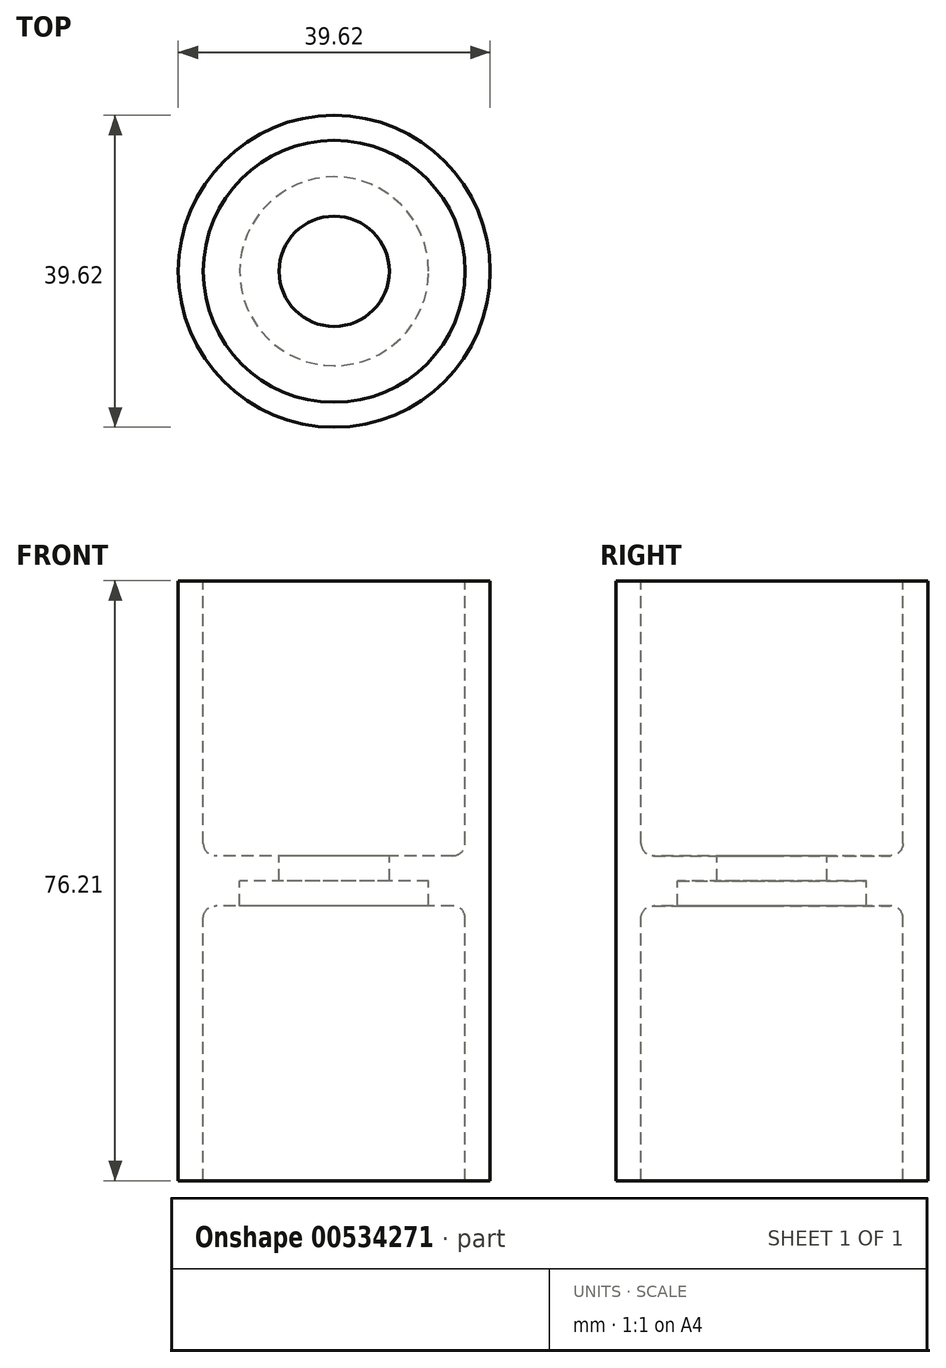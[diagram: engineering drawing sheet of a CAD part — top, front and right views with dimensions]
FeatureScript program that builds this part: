
annotation { "Feature Type Name" : "Feature", "Feature Type Description" : "" }
export const myFeature = defineFeature(function(context is Context, id is Id, definition is map)
    precondition{}
    {
        {
            var Q0;
            Q0=qCreatedBy(makeId("Front.planeOp"),FACE);
            var sketch = newSketch(context, id + "F0", { "sketchPlane" : qUnion([Q0])});
            skLineSegment(sketch, "E0", {"start": v(0, 40.97) * mm, "end": v(0, -48.47) * mm, "construction": true});
            skLineSegment(sketch, "E1", {"start": v(-19.81, 41.28) * mm, "end": v(-16.64, 41.28) * mm});
            skLineSegment(sketch, "E2", {"start": v(-16.64, 41.27) * mm, "end": v(-16.64, 7.94) * mm});
            skLineSegment(sketch, "E3", {"start": v(-15.05, 6.35) * mm, "end": v(-7, 6.35) * mm});
            skLineSegment(sketch, "E4", {"start": v(-7, 6.35) * mm, "end": v(-7, 3.18) * mm});
            skLineSegment(sketch, "E5", {"start": v(-7, 3.18) * mm, "end": v(-12, 3.17) * mm});
            skLineSegment(sketch, "E6", {"start": v(-12, 3.18) * mm, "end": v(-12, 0) * mm});
            skLineSegment(sketch, "E7", {"start": v(-12, 0) * mm, "end": v(-15.05, 0) * mm});
            skLineSegment(sketch, "E8", {"start": v(-16.64, -1.59) * mm, "end": v(-16.64, -34.93) * mm});
            skLineSegment(sketch, "E9", {"start": v(-16.64, -34.92) * mm, "end": v(-19.81, -34.92) * mm});
            skLineSegment(sketch, "E10", {"start": v(-19.81, -34.92) * mm, "end": v(-19.81, 41.28) * mm});
            skPoint(sketch, "E11.visualSharp", {"position": v(-16.64, 6.35) * mm});
            skArc(sketch, "E11.filletArc", {"start": v(-16.64, 7.94) * mm, "mid": v(-16.17, 6.81) * mm, "end": v(-15.05, 6.35) * mm});
            skPoint(sketch, "E12.visualSharp", {"position": v(-16.64, 0) * mm});
            skArc(sketch, "E12.filletArc", {"start": v(-15.05, 0) * mm, "mid": v(-16.17, -0.46) * mm, "end": v(-16.64, -1.59) * mm});
            skSolve(sketch);
        }
        {
            var Q0;
            Q0=makeQuery(id+"F0.imprint","IMPRINT",FACE,{"disambiguationData":[TD([[makeQuery(id+"F0.imprint","IMPRINT",EDGE,{"derivedFrom":sQuery(id+"F0.wireOp",EDGE,"E1")}),-1.0]])]});
            var Q1;
            Q1=sQuery(id+"F0.wireOp",EDGE,"E0");
            revolve(context, id + "F1", {"entities" : qUnion([Q0]), "axis" : qUnion([Q1]), "revolveType" : RevolveType.FULL});
        }
    });
